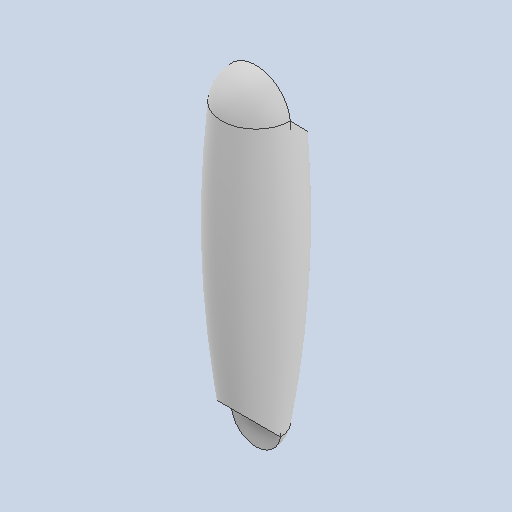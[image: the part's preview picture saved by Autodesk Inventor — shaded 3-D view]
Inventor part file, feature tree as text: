
AUTODESK INVENTOR PART (.ipt)
format: ipt  version: 2025 (Build 290162010, 162A)  size: 134,144 bytes
history: native  units: mm
features: sketch x3, extrude x2, other x1, revolve x1
ambient origin geometry x8: Origin, YZ Plane, XZ Plane, XY Plane, X Axis, Y Axis, Z Axis, Center Point
bodies: Body1 (feature_tree)
feature tree (7):
  other  "Твердое тело1"
  revolve  "Вращение1"
  extrude  "Выдавливание1"  Depth=104.0mm
  extrude  "Выдавливание2"  Depth=75.0mm
  sketch  "Эскиз1"
  sketch  "Эскиз2"
  sketch  "Эскиз3"
